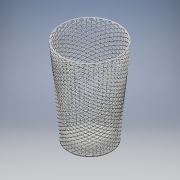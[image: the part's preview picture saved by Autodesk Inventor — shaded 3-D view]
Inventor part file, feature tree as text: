
AUTODESK INVENTOR PART (.ipt)
format: ipt  version: 2017 (Build 210142000, 142)  size: 30,178,816 bytes
history: native  units: in
note: dims shown in document units (in); Inventor stores cm internally (conversion verified against a paired STEP export)
features: sketch x3, other x2, revolve x1, extrude x1, fillet x1
ambient origin geometry x8: Origin, YZ Plane, XZ Plane, XY Plane, X Axis, Y Axis, Z Axis, Center Point
bodies: Solid1 (feature_tree)
feature tree (8):
  revolve  "Revolution1"  [1 undecoded]
  sketch  "Sketch3"  dims[d4=0.012in d5=90.0deg d6=0.3333in]
  other  "side wall"
  other  "side wall other"
  extrude  "bottom plate"  TaperAngle=90.0deg  [1 undecoded]
  fillet  "curve bottom"  Radius=0.3333in
  sketch  "Sketch2"  dims[d2=0.012in d3=0.3333in]
  sketch  "Sketch7"  dims[d7=0.012in d40=9.8425in d42=360.0deg d44=1.0in d45=1.0in d46=0.3937in d47=-0.0344in d48=90.0deg d49=90.0deg d50=0.0in d51=0.0in d52=1.0in d53=1.0in d54=0.3937in d55=-0.0344in d56=90.0deg d57=90.0deg d58=0.0in d59=0.0in d76=0.012in d77=0.0in d78=0.006in]
note: 2 required parameter values undecoded (feature->parameter linkage not recoverable at this tier; creation-order binding heuristic only, values carry confidence <= 0.55)